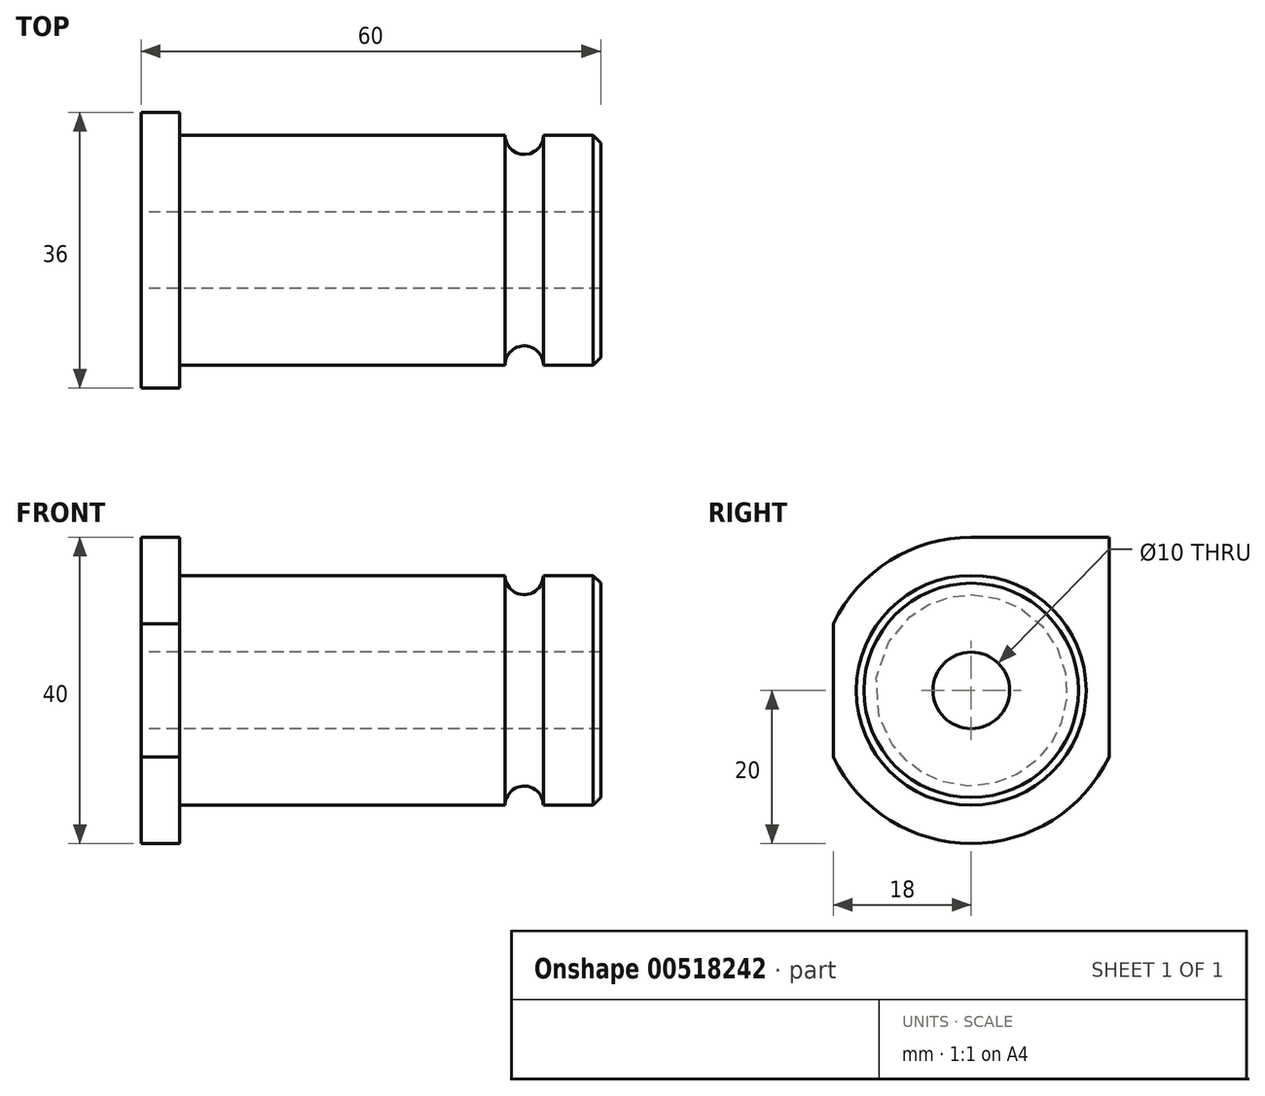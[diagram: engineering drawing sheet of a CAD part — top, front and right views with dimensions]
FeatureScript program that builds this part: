
annotation { "Feature Type Name" : "Feature", "Feature Type Description" : "" }
export const myFeature = defineFeature(function(context is Context, id is Id, definition is map)
    precondition{}
    {
        {
            var Q0;
            Q0=qCreatedBy(makeId("Top.planeOp"),FACE);
            var sketch = newSketch(context, id + "F0", { "sketchPlane" : qUnion([Q0])});
            skLineSegment(sketch, "E0", {"start": v(0, 5) * mm, "end": v(0, 15) * mm});
            skLineSegment(sketch, "E1", {"start": v(0, 15) * mm, "end": v(42.5, 15) * mm});
            skLineSegment(sketch, "E2", {"start": v(47.5, 15) * mm, "end": v(55, 15) * mm});
            skLineSegment(sketch, "E3", {"start": v(55, 15) * mm, "end": v(55, 5) * mm});
            skArc(sketch, "E4", {"start": v(42.5, 15) * mm, "mid": v(45, 12.5) * mm, "end": v(47.5, 15) * mm});
            skLineSegment(sketch, "E5", {"start": v(0, 5) * mm, "end": v(55, 5) * mm});
            skSolve(sketch);
        }
        {
            var Q0;
            Q0=qCreatedBy(makeId("Top.planeOp"),FACE);
            var sketch = newSketch(context, id + "F1", { "sketchPlane" : qUnion([Q0])});
            skLineSegment(sketch, "E6", {"start": v(-7.93, 0) * mm, "end": v(83.45, 0) * mm});
            skSolve(sketch);
        }
        {
            var Q0;
            Q0 = qSketchRegion(id + "F0", true);
            var Q1;
            Q1=sQuery(id+"F1.wireOp",EDGE,"E6");
            revolve(context, id + "F2", {"entities" : qUnion([Q0]), "axis" : qUnion([Q1]), "revolveType" : RevolveType.FULL});
        }
        {
            var Q0;
            Q0=makeQuery(id+"F2.opRevolve","SWEPT_FACE",FACE,{"disambiguationData":[OSD([sQuery(id+"F0.wireOp",EDGE,"E0")])]});
            var sketch = newSketch(context, id + "F3", { "sketchPlane" : qUnion([Q0])});
            skLineSegment(sketch, "E7.bottom", {"start": v(-18, 20) * mm, "end": v(18, 20) * mm});
            skLineSegment(sketch, "E7.top", {"start": v(-18, -20) * mm, "end": v(18, -20) * mm});
            skLineSegment(sketch, "E7.left", {"start": v(-18, 20) * mm, "end": v(-18, -20) * mm});
            skLineSegment(sketch, "E7.right", {"start": v(18, 20) * mm, "end": v(18, -20) * mm});
            skSolve(sketch);
        }
        {
            var Q0;
            Q0 = qSketchRegion(id + "F3", true);
            extrude(context, id + "F4", {"entities" : qUnion([Q0]), "operationType" : NewBodyOperationType.ADD, "depth" : 5 * mm, "offsetDistance" : 25 * mm});
        }
        {
            var Q0;
            Q0=makeQuery(id+"F4.opExtrude","CAP_FACE",FACE,{"disambiguationData":[OSD([sQuery(id+"F3.wireOp",EDGE,"E7.bottom"),sQuery(id+"F3.wireOp",EDGE,"E7.top"),sQuery(id+"F3.wireOp",EDGE,"E7.left"),sQuery(id+"F3.wireOp",EDGE,"E7.right")])],"isStart":false});
            var sketch = newSketch(context, id + "F5", { "sketchPlane" : qUnion([Q0])});
            skCircle(sketch, "E8", {"center": v(0, 0) * mm, "radius": 5 * mm});
            skArc(sketch, "E9", {"start": v(-18, 8.72) * mm, "mid": v(0, 20) * mm, "end": v(18, 8.72) * mm});
            skArc(sketch, "E10", {"start": v(-18, -8.72) * mm, "mid": v(8.72, -18) * mm, "end": v(18, 8.72) * mm});
            skSolve(sketch);
        }
        {
            var Q0;
            Q0 = qSketchRegion(id + "F5", true);
            var Q1;
            {var subQ0=sQuery(id+"F5.wireOp",EDGE,"E9");var subQ1=makeQuery(id+"F4.opExtrude","CAP_EDGE",EDGE,{"disambiguationData":[OSD([sQuery(id+"F3.wireOp",EDGE,"E7.left")])],"isStart":false});var subQ2=makeQuery(id+"F5.imprint","INTERSECT",VERTEX,{"derivedFrom":[subQ1,subQ0]});Q1=makeQuery(id+"F5.imprint","IMPRINT",FACE,{"disambiguationData":[TD([[makeQuery(id+"F5.imprint","IMPRINT",EDGE,{"disambiguationData":[TD([[subQ2,-1.0]])],"derivedFrom":subQ0}),1.0]])]});}
            var Q2;
            {var subQ0=sQuery(id+"F5.wireOp",EDGE,"E10");var subQ1=makeQuery(id+"F4.opExtrude","CAP_EDGE",EDGE,{"disambiguationData":[OSD([sQuery(id+"F3.wireOp",EDGE,"E7.left")])],"isStart":false});var subQ2=makeQuery(id+"F5.imprint","INTERSECT",VERTEX,{"derivedFrom":[subQ1,subQ0]});Q2=makeQuery(id+"F5.imprint","IMPRINT",FACE,{"disambiguationData":[TD([[makeQuery(id+"F5.imprint","IMPRINT",EDGE,{"disambiguationData":[TD([[subQ2,-1.0]])],"derivedFrom":subQ0}),-1.0]])]});}
            var Q3;
            {var subQ0=sQuery(id+"F5.wireOp",EDGE,"E10");var subQ1=makeQuery(id+"F4.opExtrude","CAP_EDGE",EDGE,{"disambiguationData":[OSD([sQuery(id+"F3.wireOp",EDGE,"E7.top")])],"isStart":false});var subQ2=makeQuery(id+"F5.imprint","INTERSECT",VERTEX,{"derivedFrom":[subQ1,subQ0]});Q3=makeQuery(id+"F5.imprint","IMPRINT",FACE,{"disambiguationData":[TD([[makeQuery(id+"F5.imprint","IMPRINT",EDGE,{"disambiguationData":[TD([[subQ2,-1.0]])],"derivedFrom":subQ0}),-1.0]])]});}
            var Q4;
            {var subQ1=makeQuery(id+"F4.opExtrude","CAP_EDGE",EDGE,{"disambiguationData":[OSD([sQuery(id+"F3.wireOp",EDGE,"E7.right")])],"isStart":false});var subQ3=makeQuery(id+"F4.opExtrude","CAP_EDGE",EDGE,{"disambiguationData":[OSD([sQuery(id+"F3.wireOp",EDGE,"E7.bottom")])],"isStart":false});var subQ5=makeQuery(id+"F5.imprint","INTERSECT",VERTEX,{"derivedFrom":[subQ3,subQ1]});Q4=makeQuery(id+"F5.imprint","IMPRINT",FACE,{"disambiguationData":[TD([[makeQuery(id+"F5.imprint","IMPRINT",EDGE,{"disambiguationData":[TD([[subQ5,1.0]])],"derivedFrom":subQ3}),-1.0]])]});}
            extrude(context, id + "F6", {"entities" : qUnion([Q0, Q1, Q2, Q3, Q4]), "operationType" : NewBodyOperationType.REMOVE, "endBound" : BoundingType.THROUGH_ALL, "oppositeDirection" : true, "depth" : 25 * mm, "offsetDistance" : 25 * mm});
        }
        {
            var Q0;
            Q0=makeQuery(id+"F2.opRevolve","SWEPT_EDGE",EDGE,{"disambiguationData":[OSD([sQuery(id+"F0.wireOp",EDGE,"E2"),sQuery(id+"F0.wireOp",EDGE,"E3")])]});
            chamfer(context, id + "F7", {"entities" : qUnion([Q0]), "width" : 1 * mm, "tangentPropagation" : true});
        }
    });
